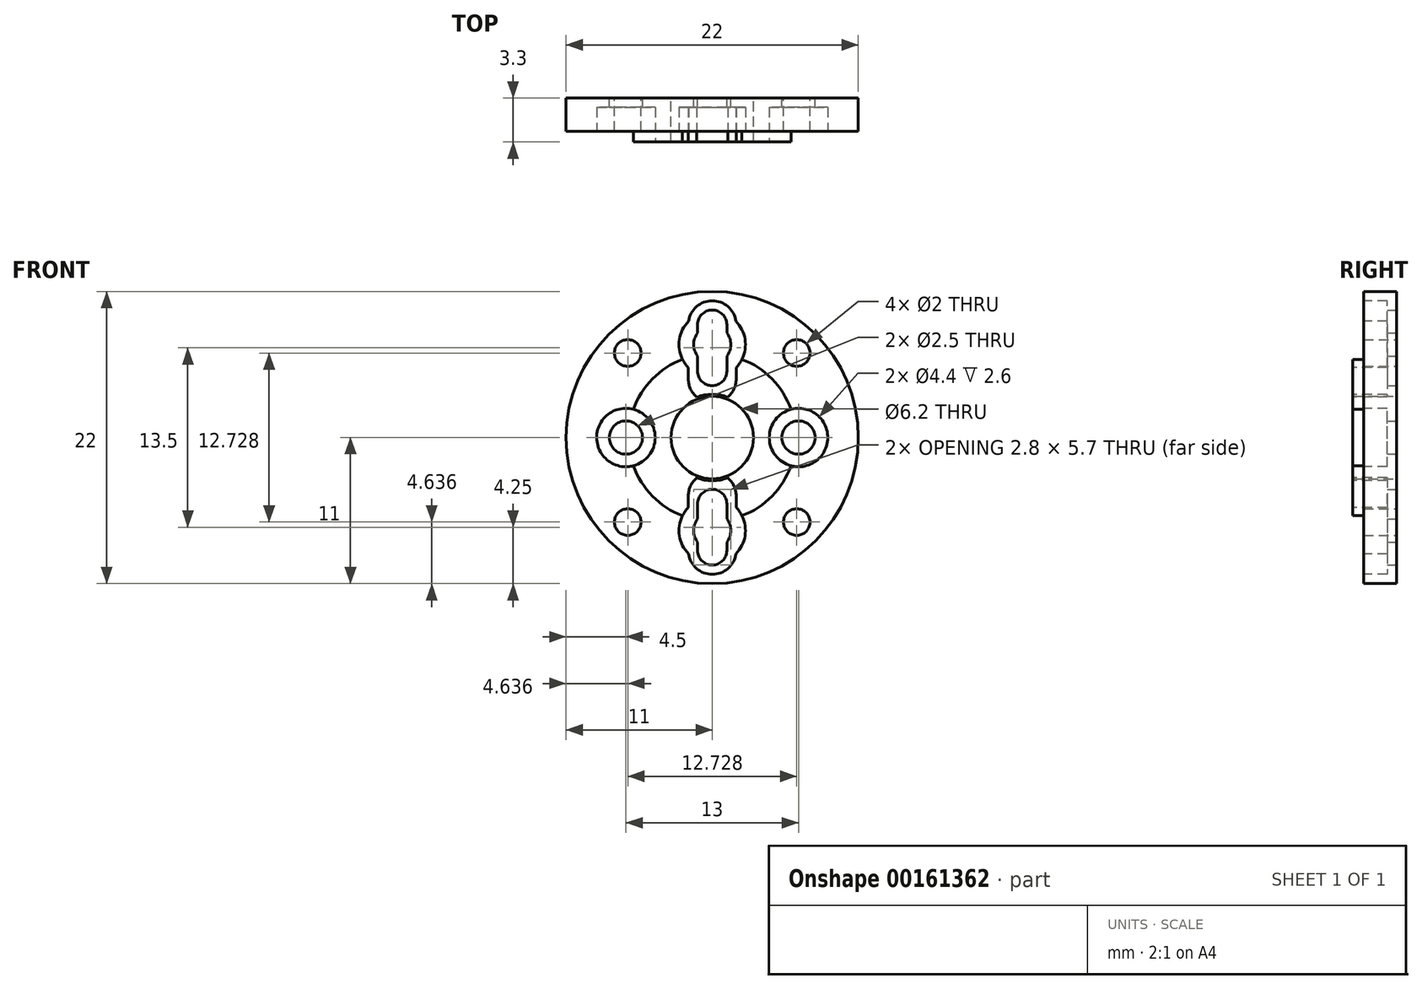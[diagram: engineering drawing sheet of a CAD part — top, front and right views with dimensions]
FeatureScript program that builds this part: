
annotation { "Feature Type Name" : "Feature", "Feature Type Description" : "" }
export const myFeature = defineFeature(function(context is Context, id is Id, definition is map)
    precondition{}
    {
        {
            var Q0;
            Q0=qCreatedBy(makeId("Front.planeOp"),FACE);
            var sketch = newSketch(context, id + "F0", { "sketchPlane" : qUnion([Q0])});
            skCircle(sketch, "E0", {"center": v(0, 0) * mm, "radius": 11 * mm});
            skSolve(sketch);
        }
        {
            var Q0;
            Q0=qCreatedBy(makeId("Front.planeOp"),FACE);
            var sketch = newSketch(context, id + "F1", { "sketchPlane" : qUnion([Q0])});
            skCircle(sketch, "E1", {"center": v(0, 0) * mm, "radius": 3.1 * mm});
            skLineSegment(sketch, "E2", {"start": v(0, 34) * mm, "end": v(0, -40.73) * mm, "construction": true});
            skLineSegment(sketch, "E3", {"start": v(35.1, 0) * mm, "end": v(-39.8, 0) * mm, "construction": true});
            skCircle(sketch, "E4", {"center": v(-6.5, 0) * mm, "radius": 1.25 * mm});
            skLineSegment(sketch, "E5", {"start": v(0, 0) * mm, "end": v(-31, 31) * mm, "construction": true});
            skCircle(sketch, "E6", {"center": v(-6.36, 6.36) * mm, "radius": 1 * mm});
            skPoint(sketch, "E7.center", {"position": v(0, -2.77) * mm});
            skCircle(sketch, "E8.1.0", {"center": v(-6.36, -6.36) * mm, "radius": 1 * mm});
            skCircle(sketch, "E8.2.0", {"center": v(6.36, -6.36) * mm, "radius": 1 * mm});
            skCircle(sketch, "E8.3.0", {"center": v(6.36, 6.36) * mm, "radius": 1 * mm});
            skCircle(sketch, "E9", {"center": v(6.5, 0) * mm, "radius": 1.25 * mm});
            skLineSegment(sketch, "E10.left", {"start": v(-1.1, -5) * mm, "end": v(-1.1, -6.13) * mm});
            skLineSegment(sketch, "E10.right", {"start": v(1.1, -5) * mm, "end": v(1.1, -6.13) * mm});
            skArc(sketch, "E11", {"start": v(-1.1, -8.5) * mm, "mid": v(0, -9.6) * mm, "end": v(1.1, -8.5) * mm});
            skArc(sketch, "E12", {"start": v(1.1, -5) * mm, "mid": v(0, -3.9) * mm, "end": v(-1.1, -5) * mm});
            skArc(sketch, "E13", {"start": v(-1.1, 7.87) * mm, "mid": v(-1.4, 7) * mm, "end": v(-1.1, 6.13) * mm});
            skPoint(sketch, "E13.centerSnap0", {"position": v(-1.1, 7) * mm});
            skArc(sketch, "E14", {"start": v(-1.1, -6.13) * mm, "mid": v(-1.4, -7) * mm, "end": v(-1.1, -7.87) * mm});
            skArc(sketch, "E15.trimOffspring", {"start": v(1.1, 6.13) * mm, "mid": v(1.4, 7) * mm, "end": v(1.1, 7.87) * mm});
            skArc(sketch, "E16.trimOffspring", {"start": v(1.1, -7.87) * mm, "mid": v(1.4, -7) * mm, "end": v(1.1, -6.13) * mm});
            skLineSegment(sketch, "E17.trimOffspring", {"start": v(-1.1, -7.87) * mm, "end": v(-1.1, -8.5) * mm});
            skLineSegment(sketch, "E18.trimOffspring", {"start": v(1.1, -7.87) * mm, "end": v(1.1, -8.5) * mm});
            skLineSegment(sketch, "E19.left", {"start": v(-1.1, 8.5) * mm, "end": v(-1.1, 7.87) * mm});
            skLineSegment(sketch, "E19.right", {"start": v(1.1, 8.5) * mm, "end": v(1.1, 7.87) * mm});
            skArc(sketch, "E20", {"start": v(1.1, 8.5) * mm, "mid": v(0, 9.6) * mm, "end": v(-1.1, 8.5) * mm});
            skArc(sketch, "E21", {"start": v(-1.1, 5) * mm, "mid": v(0, 3.9) * mm, "end": v(1.1, 5) * mm});
            skLineSegment(sketch, "E22.trimOffspring", {"start": v(-1.1, 6.13) * mm, "end": v(-1.1, 5) * mm});
            skLineSegment(sketch, "E23.trimOffspring", {"start": v(1.1, 6.13) * mm, "end": v(1.1, 5) * mm});
            skSolve(sketch);
        }
        {
            var Q0;
            Q0=qSketchRegion(id+"F0",true);
            extrude(context, id + "F2", {"entities" : qUnion([Q0]), "depth" : 2.5 * mm});
        }
        {
            var Q0;
            Q0=qSketchRegion(id+"F1",true);
            extrude(context, id + "F3", {"entities" : qUnion([Q0]), "operationType" : NewBodyOperationType.REMOVE, "endBound" : BoundingType.THROUGH_ALL, "depth" : 25 * mm});
        }
        {
            var Q0;
            Q0=makeQuery(id+"F2.opExtrude","CAP_FACE",FACE,{"disambiguationData":[OSD([sQuery(id+"F0.wireOp",EDGE,"E0")])],"isStart":false});
            var sketch = newSketch(context, id + "F4", { "sketchPlane" : qUnion([Q0])});
            skPoint(sketch, "E24.center", {"position": v(0, 0) * mm});
            skCircle(sketch, "E25", {"center": v(-6.5, 0) * mm, "radius": 2.2 * mm});
            skCircle(sketch, "E26", {"center": v(6.5, 0) * mm, "radius": 2.2 * mm});
            skArc(sketch, "E27", {"start": v(1.8, 5.27) * mm, "mid": v(2.5, 7.01) * mm, "end": v(1.78, 8.75) * mm});
            skArc(sketch, "E28", {"start": v(-1.8, -5.27) * mm, "mid": v(-2.5, -7.01) * mm, "end": v(-1.78, -8.75) * mm});
            skLineSegment(sketch, "E29.left", {"start": v(-1.8, 5.27) * mm, "end": v(-1.8, 4.4) * mm});
            skLineSegment(sketch, "E29.right", {"start": v(1.8, 5.27) * mm, "end": v(1.8, 4.4) * mm});
            skArc(sketch, "E30", {"start": v(1.78, 8.75) * mm, "mid": v(0, 10.3) * mm, "end": v(-1.78, 8.75) * mm});
            skArc(sketch, "E31", {"start": v(1.17, 3.03) * mm, "mid": v(1.63, 3.65) * mm, "end": v(1.8, 4.4) * mm});
            skArc(sketch, "E32", {"start": v(1.17, 3.03) * mm, "mid": v(0, 3.25) * mm, "end": v(-1.17, 3.03) * mm});
            skLineSegment(sketch, "E33.left", {"start": v(-1.8, -4.4) * mm, "end": v(-1.8, -5.27) * mm});
            skLineSegment(sketch, "E33.right", {"start": v(1.8, -4.4) * mm, "end": v(1.8, -5.27) * mm});
            skArc(sketch, "E34", {"start": v(-1.17, -3.03) * mm, "mid": v(-1.63, -3.65) * mm, "end": v(-1.8, -4.4) * mm});
            skArc(sketch, "E35", {"start": v(-1.78, -8.75) * mm, "mid": v(0, -10.3) * mm, "end": v(1.78, -8.75) * mm});
            skArc(sketch, "E36.trimOffspring", {"start": v(-1.17, -3.03) * mm, "mid": v(0, -3.25) * mm, "end": v(1.17, -3.03) * mm});
            skArc(sketch, "E37.trimOffspring", {"start": v(1.8, -4.4) * mm, "mid": v(1.63, -3.65) * mm, "end": v(1.17, -3.03) * mm});
            skArc(sketch, "E38.trimOffspring", {"start": v(1.78, -8.75) * mm, "mid": v(2.5, -7.01) * mm, "end": v(1.8, -5.27) * mm});
            skArc(sketch, "E39.trimOffspring", {"start": v(-1.8, 4.4) * mm, "mid": v(-1.63, 3.65) * mm, "end": v(-1.17, 3.03) * mm});
            skArc(sketch, "E40.trimOffspring", {"start": v(-1.78, 8.75) * mm, "mid": v(-2.5, 7.01) * mm, "end": v(-1.8, 5.27) * mm});
            skPoint(sketch, "E41.orphan", {"position": v(1.8, 8.5) * mm});
            skPoint(sketch, "E42.orphan", {"position": v(-1.8, 8.5) * mm});
            skSolve(sketch);
        }
        {
            var Q0;
            Q0=qSketchRegion(id+"F4",true);
            extrude(context, id + "F5", {"entities" : qUnion([Q0]), "operationType" : NewBodyOperationType.REMOVE, "oppositeDirection" : true, "depth" : 1.8 * mm});
        }
        {
            var Q0;
            Q0=makeQuery(id+"F2.opExtrude","CAP_FACE",FACE,{"disambiguationData":[OSD([sQuery(id+"F0.wireOp",EDGE,"E0")])],"isStart":false});
            var sketch = newSketch(context, id + "F6", { "sketchPlane" : qUnion([Q0])});
            skCircle(sketch, "E43", {"center": v(0, 0) * mm, "radius": 6.3 * mm});
            skSolve(sketch);
        }
        {
            var Q0;
            Q0 = qSketchRegion(id + "F6", true);
            extrude(context, id + "F7", {"entities" : qUnion([Q0]), "operationType" : NewBodyOperationType.ADD, "depth" : 0.8 * mm});
        }
        {
            var Q0;
            Q0 = qSketchRegion(id + "F4", true);
            extrude(context, id + "F8", {"entities" : qUnion([Q0]), "operationType" : NewBodyOperationType.REMOVE, "depth" : 0.8 * mm});
        }
        {
            var Q0;
            Q0 = qSketchRegion(id + "F1", true);
            extrude(context, id + "F9", {"entities" : qUnion([Q0]), "operationType" : NewBodyOperationType.REMOVE, "endBound" : BoundingType.THROUGH_ALL, "depth" : 25 * mm});
        }
    });
